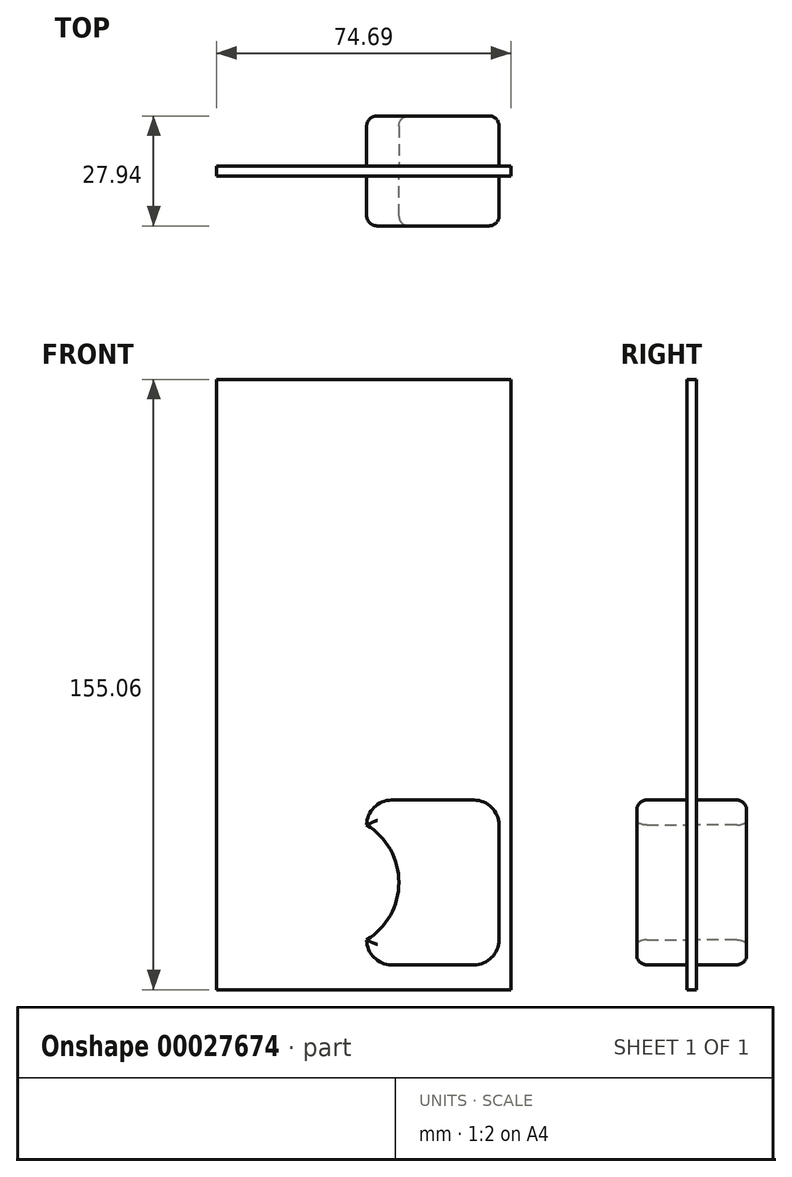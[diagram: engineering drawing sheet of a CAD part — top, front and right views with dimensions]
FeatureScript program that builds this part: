
annotation { "Feature Type Name" : "Feature", "Feature Type Description" : "" }
export const myFeature = defineFeature(function(context is Context, id is Id, definition is map)
    precondition{}
    {
        {
            var Q0;
            Q0=qCreatedBy(makeId("Front.planeOp"),FACE);
            var sketch = newSketch(context, id + "F0", { "sketchPlane" : qUnion([Q0])});
            skLineSegment(sketch, "E0", {"start": v(6.35, 0) * mm, "end": v(27.26, 0) * mm});
            skLineSegment(sketch, "E1", {"start": v(33.6, 6.35) * mm, "end": v(33.6, 35.5) * mm});
            skLineSegment(sketch, "E2", {"start": v(27.26, 41.84) * mm, "end": v(6.35, 41.84) * mm});
            skPoint(sketch, "E3.visualSharp", {"position": v(0, 41.84) * mm});
            skArc(sketch, "E3.filletArc", {"start": v(6.35, 41.84) * mm, "mid": v(1.86, 39.98) * mm, "end": v(0, 35.5) * mm});
            skPoint(sketch, "E4.visualSharp", {"position": v(0, 0) * mm});
            skArc(sketch, "E4.filletArc", {"start": v(0, 6.35) * mm, "mid": v(1.86, 1.86) * mm, "end": v(6.35, 0) * mm});
            skPoint(sketch, "E5.visualSharp", {"position": v(33.6, 0) * mm});
            skArc(sketch, "E5.filletArc", {"start": v(27.26, 0) * mm, "mid": v(31.75, 1.86) * mm, "end": v(33.6, 6.35) * mm});
            skPoint(sketch, "E6.visualSharp", {"position": v(33.6, 41.84) * mm});
            skArc(sketch, "E6.filletArc", {"start": v(33.6, 35.5) * mm, "mid": v(31.75, 39.98) * mm, "end": v(27.26, 41.84) * mm});
            skArc(sketch, "E7", {"start": v(0, 6.35) * mm, "mid": v(8.19, 20.92) * mm, "end": v(0, 35.5) * mm});
            skSolve(sketch);
        }
        {
            var Q0;
            Q0 = qSketchRegion(id + "F0", true);
            extrude(context, id + "F1", {"entities" : qUnion([Q0]), "depth" : 12.7 * mm});
        }
        {
            var Q0;
            Q0=qCreatedBy(makeId("Front.planeOp"),FACE);
            var sketch = newSketch(context, id + "F2", { "sketchPlane" : qUnion([Q0])});
            skLineSegment(sketch, "E8.bottom", {"start": v(36.6, -6.32) * mm, "end": v(-38.09, -6.32) * mm});
            skLineSegment(sketch, "E8.top", {"start": v(36.6, 148.74) * mm, "end": v(-38.09, 148.74) * mm});
            skLineSegment(sketch, "E8.left", {"start": v(36.6, -6.32) * mm, "end": v(36.6, 148.74) * mm});
            skLineSegment(sketch, "E8.right", {"start": v(-38.09, -6.32) * mm, "end": v(-38.09, 148.74) * mm});
            skSolve(sketch);
        }
        {
            var Q0;
            Q0 = qSketchRegion(id + "F2", true);
            extrude(context, id + "F3", {"entities" : qUnion([Q0]), "oppositeDirection" : true, "depth" : 2.54 * mm});
        }
        {
            var Q0;
            Q0=makeQuery(id+"F3.opExtrude","SWEPT_FACE",FACE,{"disambiguationData":[OSD([sQuery(id+"F2.wireOp",EDGE,"E8.left")])]});
            var sketch = newSketch(context, id + "F4", { "sketchPlane" : qUnion([Q0])});
            skPoint(sketch, "E9", {"position": v(1.27, -6.32) * mm});
            skSolve(sketch);
        }
        {
            var Q0;
            Q0=sQuery(id+"F4.wireOp",VERTEX,"E9");
            var Q1;
            Q1=qCreatedBy(makeId("Front.planeOp"),FACE);
            cPlane(context, id + "F5", {"entities" : qUnion([Q0, Q1]), "cplaneType" : CPlaneType.PLANE_POINT, "offset" : 25.4 * mm, "width" : 152.4 * mm, "height" : 152.4 * mm});
        }
        {
            var Q0;
            Q0=makeQuery(id+"F1.opExtrude","CAP_EDGE",EDGE,{"disambiguationData":[OSD([sQuery(id+"F0.wireOp",EDGE,"E0")])],"isStart":false});
            var Q1;
            Q1=makeQuery(id+"F1.opExtrude","CAP_EDGE",EDGE,{"disambiguationData":[OSD([sQuery(id+"F0.wireOp",EDGE,"E5.filletArc")])],"isStart":false});
            var Q2;
            Q2=makeQuery(id+"F1.opExtrude","CAP_EDGE",EDGE,{"disambiguationData":[OSD([sQuery(id+"F0.wireOp",EDGE,"E1")])],"isStart":false});
            var Q3;
            Q3=makeQuery(id+"F1.opExtrude","CAP_EDGE",EDGE,{"disambiguationData":[OSD([sQuery(id+"F0.wireOp",EDGE,"E6.filletArc")])],"isStart":false});
            var Q4;
            Q4=makeQuery(id+"F1.opExtrude","CAP_EDGE",EDGE,{"disambiguationData":[OSD([sQuery(id+"F0.wireOp",EDGE,"E2")])],"isStart":false});
            var Q5;
            Q5=makeQuery(id+"F1.opExtrude","CAP_EDGE",EDGE,{"disambiguationData":[OSD([sQuery(id+"F0.wireOp",EDGE,"E3.filletArc")])],"isStart":false});
            var Q6;
            Q6=makeQuery(id+"F1.opExtrude","CAP_EDGE",EDGE,{"disambiguationData":[OSD([sQuery(id+"F0.wireOp",EDGE,"E7")])],"isStart":false});
            var Q7;
            Q7=makeQuery(id+"F1.opExtrude","CAP_EDGE",EDGE,{"disambiguationData":[OSD([sQuery(id+"F0.wireOp",EDGE,"E4.filletArc")])],"isStart":false});
            fillet(context, id + "F6", {"entities" : qUnion([Q0, Q1, Q2, Q3, Q4, Q5, Q6, Q7]), "radius" : 2.54 * mm, "tangentPropagation" : true, "allowEdgeOverflow" : false});
        }
        {
            var Q0;
            Q0=makeQuery(id+"F1.opExtrude","SWEPT_BODY",BODY,{"disambiguationData":[OSD([sQuery(id+"F0.wireOp",EDGE,"E0"),sQuery(id+"F0.wireOp",EDGE,"E1"),sQuery(id+"F0.wireOp",EDGE,"E2"),sQuery(id+"F0.wireOp",EDGE,"E3.filletArc"),sQuery(id+"F0.wireOp",EDGE,"E4.filletArc"),sQuery(id+"F0.wireOp",EDGE,"E5.filletArc"),sQuery(id+"F0.wireOp",EDGE,"E6.filletArc"),sQuery(id+"F0.wireOp",EDGE,"E7")])]});
            var Q1;
            Q1=qCreatedBy(id+"F5.planeOp",FACE);
            mirror(context, id + "F7", {"entities" : qUnion([Q0]), "mirrorPlane" : qUnion([Q1])});
        }
    });
